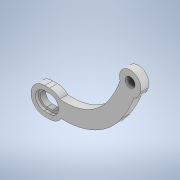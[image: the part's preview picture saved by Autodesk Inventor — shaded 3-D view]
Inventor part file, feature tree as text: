
AUTODESK INVENTOR PART (.ipt)
format: ipt  version: 2020.3 (Build 243373000, 373)  size: 236,032 bytes
history: native  units: in
note: dims shown in document units (in); Inventor stores cm internally (conversion verified against a paired STEP export)
features: extrude x9, sketch x6, projected_geometry x3
ambient origin geometry x8: Origin, YZ Plane, XZ Plane, XY Plane, X Axis, Y Axis, Z Axis, Center Point
bodies: Solid1 (feature_tree)
feature tree (18):
  extrude  "Extrusion1"  Depth=0.0984in
  extrude  "Extrusion3"  Depth=0.8661in
  sketch  "Sketch4"  dims[d25=0.1181in d26=0.0in d31=0.3937in]
  extrude  "Extrusion4"  Depth=0.3937in
  sketch  "Sketch5"  dims[d32=0.0394in d33=0.0394in]
  extrude  "Extrusion5"  Depth=0.0394in
  extrude  "Extrusion6"  Depth=0.3937in TaperAngle=0.0deg
  extrude  "Extrusion7"  Depth=0.3937in
  extrude  "Extrusion8"  Depth=0.3937in
  sketch  "Sketch7"  dims[d43=0.1969in d44=0.315in d46=0.0103in d47=0.1417in d48=0.3937in d49=0.0in d50=0.1969in d51=0.0in d52=0.0315in d53=0.0394in d54=0.0in d55=0.3937in d56=0.0in d57=0.3937in d58=0.0in d59=0.3937in d60=0.0in]
  extrude  "Extrusion9"  Depth=0.3937in
  extrude  "Extrusion10"  Depth=0.3937in TaperAngle=0.0deg
  sketch  "Sketch1"  dims[d1=1.1811in d21=0.2362in d22=0.0984in]
  sketch  "Sketch3"  dims[d23=1.2205in d24=0.8661in]
  projected_geometry  "Projected Loop1"
  sketch  "Sketch6"  dims[d34=0.1181in d35=0.1575in d36=0.0in d37=0.0in d40=0.3937in d41=0.0in]
  projected_geometry  "Projected Loop2"
  projected_geometry  "Projected Loop3"
